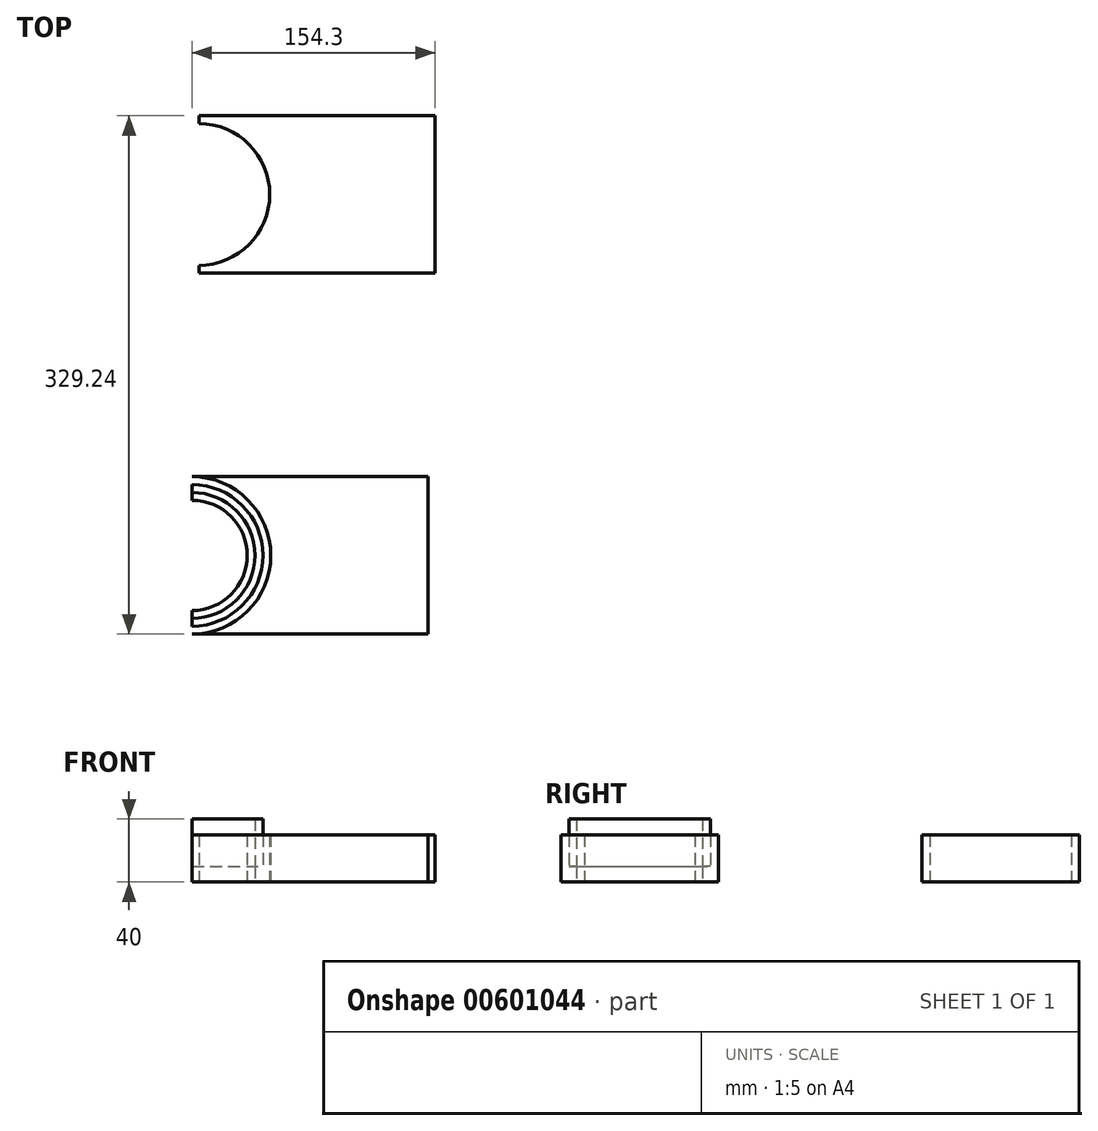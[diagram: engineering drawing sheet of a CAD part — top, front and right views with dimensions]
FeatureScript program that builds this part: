
annotation { "Feature Type Name" : "Feature", "Feature Type Description" : "" }
export const myFeature = defineFeature(function(context is Context, id is Id, definition is map)
    precondition{}
    {
        {
            var Q0;
            Q0=qCreatedBy(makeId("Top.planeOp"),FACE);
            var sketch = newSketch(context, id + "F0", { "sketchPlane" : qUnion([Q0])});
            skLineSegment(sketch, "E0.bottom", {"start": v(-73.78, 61.01) * mm, "end": v(76.22, 61.01) * mm});
            skLineSegment(sketch, "E0.top", {"start": v(-73.78, -38.99) * mm, "end": v(76.22, -38.99) * mm});
            skLineSegment(sketch, "E0.left", {"start": v(-73.78, 61.01) * mm, "end": v(-73.78, -38.99) * mm});
            skLineSegment(sketch, "E0.right", {"start": v(76.22, 61.01) * mm, "end": v(76.22, -38.99) * mm});
            skLineSegment(sketch, "E1.bottom", {"start": v(-78.08, -168.23) * mm, "end": v(71.92, -168.23) * mm});
            skLineSegment(sketch, "E1.top", {"start": v(-78.08, -268.23) * mm, "end": v(71.92, -268.23) * mm});
            skLineSegment(sketch, "E1.left", {"start": v(-78.08, -168.23) * mm, "end": v(-78.08, -268.23) * mm});
            skLineSegment(sketch, "E1.right", {"start": v(71.92, -168.23) * mm, "end": v(71.92, -268.23) * mm});
            skArc(sketch, "E2", {"start": v(-78.08, -168.23) * mm, "mid": v(-28.08, -218.23) * mm, "end": v(-78.08, -268.23) * mm});
            skArc(sketch, "E3", {"start": v(-73.78, -38.99) * mm, "mid": v(-23.78, 11.01) * mm, "end": v(-73.78, 61.01) * mm});
            skPoint(sketch, "E4", {"position": v(-73.78, -28.99) * mm});
            skPoint(sketch, "E5", {"position": v(-73.78, -23.99) * mm});
            skArc(sketch, "E6", {"start": v(-73.78, -28.99) * mm, "mid": v(-33.78, 11.01) * mm, "end": v(-73.78, 51.01) * mm});
            skArc(sketch, "E7", {"start": v(-73.78, -23.99) * mm, "mid": v(-38.78, 11.01) * mm, "end": v(-73.78, 46.01) * mm});
            skPoint(sketch, "E8", {"position": v(-73.78, -33.99) * mm});
            skArc(sketch, "E9", {"start": v(-73.78, -33.99) * mm, "mid": v(-28.78, 11.01) * mm, "end": v(-73.78, 56.01) * mm});
            skPoint(sketch, "E10", {"position": v(-78.08, -263.23) * mm});
            skPoint(sketch, "E11", {"position": v(-78.08, -258.23) * mm});
            skPoint(sketch, "E12", {"position": v(-78.08, -253.23) * mm});
            skArc(sketch, "E13", {"start": v(-78.08, -263.23) * mm, "mid": v(-33.08, -218.23) * mm, "end": v(-78.08, -173.23) * mm});
            skArc(sketch, "E14", {"start": v(-78.08, -258.23) * mm, "mid": v(-38.08, -218.23) * mm, "end": v(-78.08, -178.23) * mm});
            skArc(sketch, "E15", {"start": v(-78.08, -253.23) * mm, "mid": v(-43.08, -218.23) * mm, "end": v(-78.08, -183.23) * mm});
            skSolve(sketch);
        }
        {
            var Q0;
            {var subQ0=sQuery(id+"F0.wireOp",EDGE,"E14");Q0=makeQuery(id+"F0.imprint","IMPRINT",FACE,{"disambiguationData":[TD([[makeQuery(id+"F0.imprint","IMPRINT",EDGE,{"derivedFrom":subQ0}),1.0]])]});}
            var Q1;
            {var subQ0=sQuery(id+"F0.wireOp",EDGE,"E2");Q1=makeQuery(id+"F0.imprint","IMPRINT",FACE,{"disambiguationData":[TD([[makeQuery(id+"F0.imprint","IMPRINT",EDGE,{"derivedFrom":subQ0}),-1.0]])]});}
            var Q2;
            {var subQ0=sQuery(id+"F0.wireOp",EDGE,"E13");Q2=makeQuery(id+"F0.imprint","IMPRINT",FACE,{"disambiguationData":[TD([[makeQuery(id+"F0.imprint","IMPRINT",EDGE,{"derivedFrom":subQ0}),1.0]])]});}
            var Q3;
            Q3=makeQuery(id+"F0.imprint","IMPRINT",FACE,{"disambiguationData":[TD([[makeQuery(id+"F0.imprint","IMPRINT",EDGE,{"derivedFrom":sQuery(id+"F0.wireOp",EDGE,"E1.bottom")}),-1.0]])]});
            var Q4;
            Q4=makeQuery(id+"F0.imprint","IMPRINT",FACE,{"disambiguationData":[TD([[makeQuery(id+"F0.imprint","IMPRINT",EDGE,{"derivedFrom":sQuery(id+"F0.wireOp",EDGE,"E0.bottom")}),-1.0]])]});
            var Q5;
            {var subQ0=sQuery(id+"F0.wireOp",EDGE,"E3");Q5=makeQuery(id+"F0.imprint","IMPRINT",FACE,{"disambiguationData":[TD([[makeQuery(id+"F0.imprint","IMPRINT",EDGE,{"derivedFrom":subQ0}),1.0]])]});}
            var Q6;
            {var subQ0=sQuery(id+"F0.wireOp",EDGE,"E6");Q6=makeQuery(id+"F0.imprint","IMPRINT",FACE,{"disambiguationData":[TD([[makeQuery(id+"F0.imprint","IMPRINT",EDGE,{"derivedFrom":subQ0}),-1.0]])]});}
            var Q7;
            {var subQ0=sQuery(id+"F0.wireOp",EDGE,"E6");Q7=makeQuery(id+"F0.imprint","IMPRINT",FACE,{"disambiguationData":[TD([[makeQuery(id+"F0.imprint","IMPRINT",EDGE,{"derivedFrom":subQ0}),1.0]])]});}
            extrude(context, id + "F1", {"entities" : qUnion([Q0, Q1, Q2, Q3, Q4, Q5, Q6, Q7]), "depth" : 30 * mm, "offsetDistance" : 25 * mm});
        }
        {
            var Q0;
            {var subQ0=sQuery(id+"F0.wireOp",EDGE,"E13");Q0=makeQuery(id+"F0.imprint","IMPRINT",FACE,{"disambiguationData":[TD([[makeQuery(id+"F0.imprint","IMPRINT",EDGE,{"derivedFrom":subQ0}),1.0]])]});}
            var Q1;
            {var subQ0=sQuery(id+"F0.wireOp",EDGE,"E6");Q1=makeQuery(id+"F0.imprint","IMPRINT",FACE,{"disambiguationData":[TD([[makeQuery(id+"F0.imprint","IMPRINT",EDGE,{"derivedFrom":subQ0}),-1.0]])]});}
            extrude(context, id + "F2", {"entities" : qUnion([Q0, Q1]), "depth" : 40 * mm, "offsetDistance" : 25 * mm});
        }
        {
            var Q0;
            {var subQ0=sQuery(id+"F0.wireOp",EDGE,"E13");Q0=makeQuery(id+"F0.imprint","IMPRINT",FACE,{"disambiguationData":[TD([[makeQuery(id+"F0.imprint","IMPRINT",EDGE,{"derivedFrom":subQ0}),1.0]])]});}
            var Q1;
            {var subQ0=sQuery(id+"F0.wireOp",EDGE,"E6");Q1=makeQuery(id+"F0.imprint","IMPRINT",FACE,{"disambiguationData":[TD([[makeQuery(id+"F0.imprint","IMPRINT",EDGE,{"derivedFrom":subQ0}),-1.0]])]});}
            extrude(context, id + "F3", {"entities" : qUnion([Q0, Q1]), "operationType" : NewBodyOperationType.REMOVE, "depth" : 10 * mm, "offsetDistance" : 25 * mm});
        }
    });
